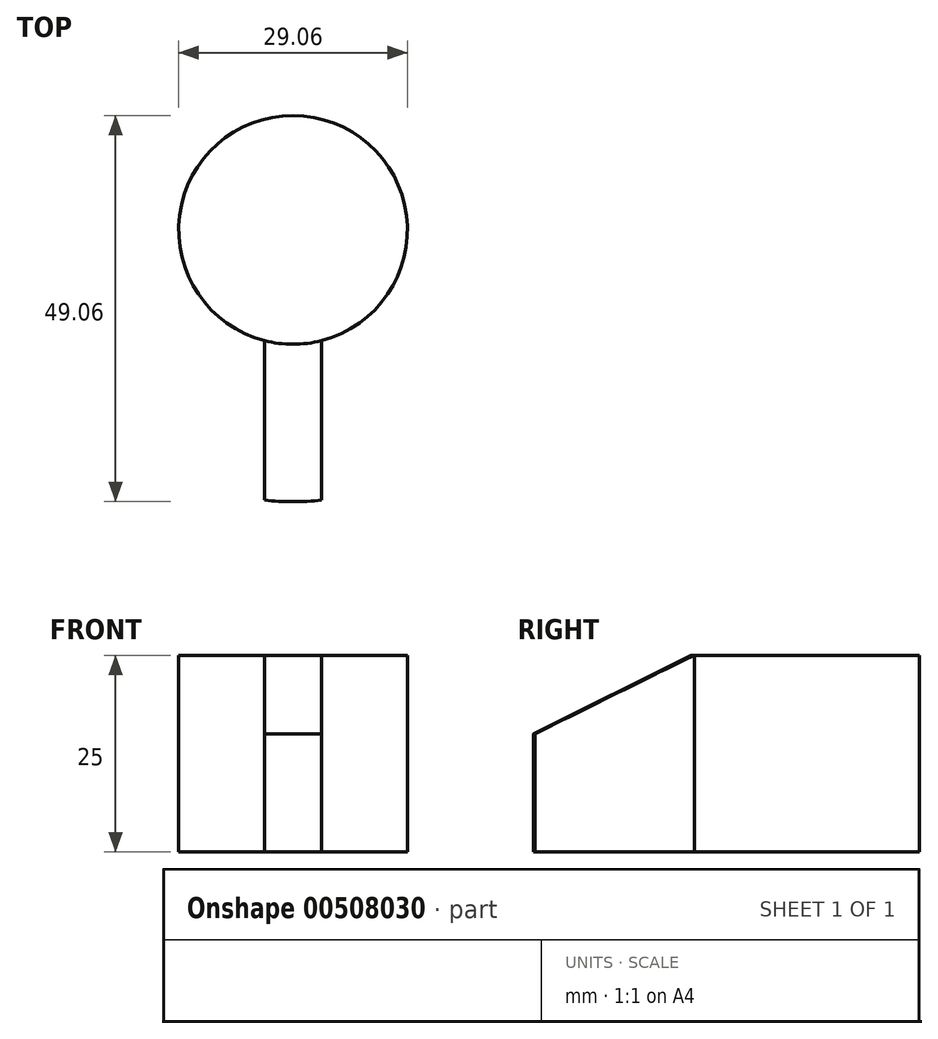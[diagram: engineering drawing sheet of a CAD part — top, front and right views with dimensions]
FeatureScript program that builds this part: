
annotation { "Feature Type Name" : "Feature", "Feature Type Description" : "" }
export const myFeature = defineFeature(function(context is Context, id is Id, definition is map)
    precondition{}
    {
        {
            var Q0;
            Q0=qCreatedBy(makeId("Top.planeOp"),FACE);
            var sketch = newSketch(context, id + "F0", { "sketchPlane" : qUnion([Q0])});
            skCircle(sketch, "E0", {"center": v(0, 0) * mm, "radius": 34.53 * mm});
            skSolve(sketch);
        }
        {
            var Q0;
            Q0 = qSketchRegion(id + "F0", true);
            extrude(context, id + "F1", {"entities" : qUnion([Q0]), "depth" : 25 * mm, "offsetDistance" : 25 * mm});
        }
        {
            var Q0;
            Q0=makeQuery(id+"F1.opExtrude","CAP_EDGE",EDGE,{"disambiguationData":[OSD([sQuery(id+"F0.wireOp",EDGE,"E0")])],"isStart":false});
            chamfer(context, id + "F2", {"entities" : qUnion([Q0]), "chamferType" : ChamferType.TWO_OFFSETS, "width1" : 20 * mm, "oppositeDirection" : false, "width2" : 10 * mm, "tangentPropagation" : true});
        }
        {
            var Q0;
            Q0=makeQuery(id+"F1.opExtrude","CAP_FACE",FACE,{"disambiguationData":[OSD([sQuery(id+"F0.wireOp",EDGE,"E0")])],"isStart":false});
            var sketch = newSketch(context, id + "F3", { "sketchPlane" : qUnion([Q0])});
            skLineSegment(sketch, "E1", {"start": v(-3.62, -14.07) * mm, "end": v(-3.62, -34.34) * mm});
            skLineSegment(sketch, "E2", {"start": v(3.62, -14.07) * mm, "end": v(3.62, -34.34) * mm});
            skLineSegment(sketch, "E3", {"start": v(0, 0) * mm, "end": v(0, -56.15) * mm, "construction": true});
            skCircle(sketch, "E4.0", {"center": v(0, 0) * mm, "radius": 34.53 * mm});
            skSolve(sketch);
        }
        {
            var Q0;
            {var subQ0=sQuery(id+"F3.wireOp",EDGE,"E1");Q0=makeQuery(id+"F3.imprint","IMPRINT",FACE,{"disambiguationData":[TD([[makeQuery(id+"F3.imprint","IMPRINT",EDGE,{"derivedFrom":subQ0}),-1.0]])]});}
            extrude(context, id + "F4", {"entities" : qUnion([Q0]), "operationType" : NewBodyOperationType.REMOVE, "oppositeDirection" : true, "depth" : 25 * mm, "offsetDistance" : 25 * mm});
        }
    });
